# Revit family: Kombiableiter V50, 1-polig mit FS
name_source: partatom
category: Generic Models
revit_build: Autodesk Revit 2015 (Build: 20140606_1530(x64)
units: mm (PartAtom-declared; Revit-internal decimal feet)

## types (4) — shared parameters
Height = 79 mm
Length = 18 mm
Manufacturer = OBO Bettermann
Material = PA 66/6 FR HF RAL 9010
Material 2 = PA 66/6 FR HF RAL 2003
URL = http://www.obo-bettermann.com
Width = 90 mm  [stored 0.295276 ft]

## per-type parameters (varying)
| type | GTIN | Manufacturer Art.No. |
| V50-1+FS-280 | 4012196412969 | 5093502 |
| V50-1+FS-320 | 4012196398454 | 5093546 |
| V50-1+FS-150 | 4012196398645 | 5093446 |
| V50-1+FS-385 | 4012196398560 | 5093578 |

note: column(s) folded — value = type name in every type: Article Type

note: [stored X ft] marks values corroborated as IEEE doubles in the binary element streams (Revit-internal decimal feet)

## geometry (parser evidence)
native form markers: Sweep x2
no freeform markers — native parametric forms only
